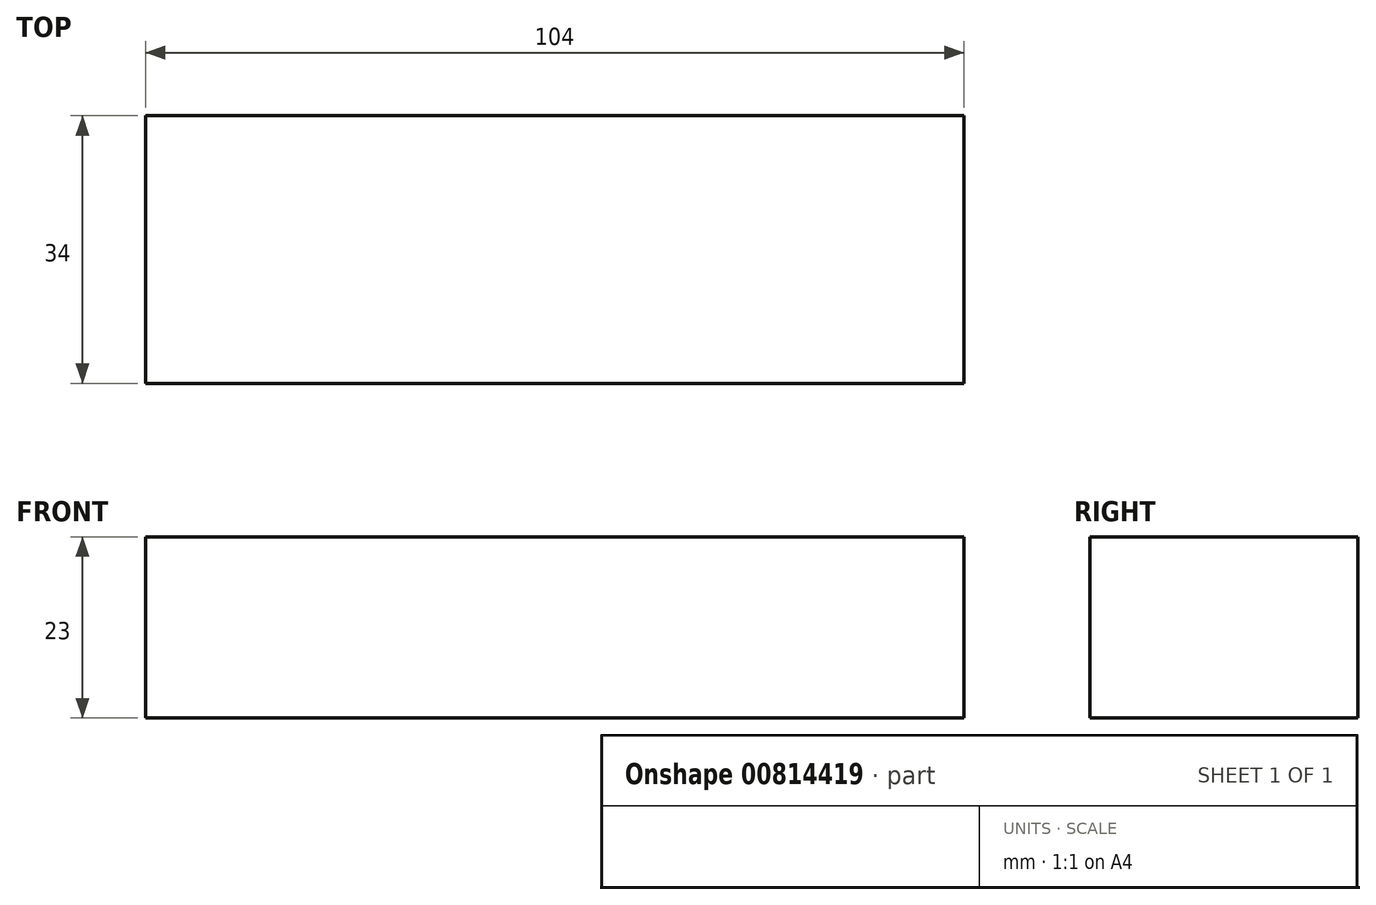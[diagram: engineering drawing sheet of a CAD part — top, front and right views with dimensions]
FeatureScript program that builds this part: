
annotation { "Feature Type Name" : "Feature", "Feature Type Description" : "" }
export const myFeature = defineFeature(function(context is Context, id is Id, definition is map)
    precondition{}
    {
        {
            var Q0;
            Q0=qCreatedBy(makeId("Top.planeOp"),FACE);
            var sketch = newSketch(context, id + "F0", { "sketchPlane" : qUnion([Q0])});
            skLineSegment(sketch, "E0.bottom", {"start": v(0, 0) * mm, "end": v(104, 0) * mm});
            skLineSegment(sketch, "E0.top", {"start": v(0, -34) * mm, "end": v(104, -34) * mm});
            skLineSegment(sketch, "E0.left", {"start": v(0, 0) * mm, "end": v(0, -34) * mm});
            skLineSegment(sketch, "E0.right", {"start": v(104, 0) * mm, "end": v(104, -34) * mm});
            skSolve(sketch);
        }
        {
            var Q0;
            Q0=makeQuery(id+"F0.imprint","IMPRINT",FACE,{"disambiguationData":[TD([[makeQuery(id+"F0.imprint","IMPRINT",EDGE,{"derivedFrom":sQuery(id+"F0.wireOp",EDGE,"E0.bottom")}),-1.0]])]});
            extrude(context, id + "F1", {"entities" : qUnion([Q0]), "depth" : 23 * mm, "offsetDistance" : 25.4 * mm});
        }
    });
